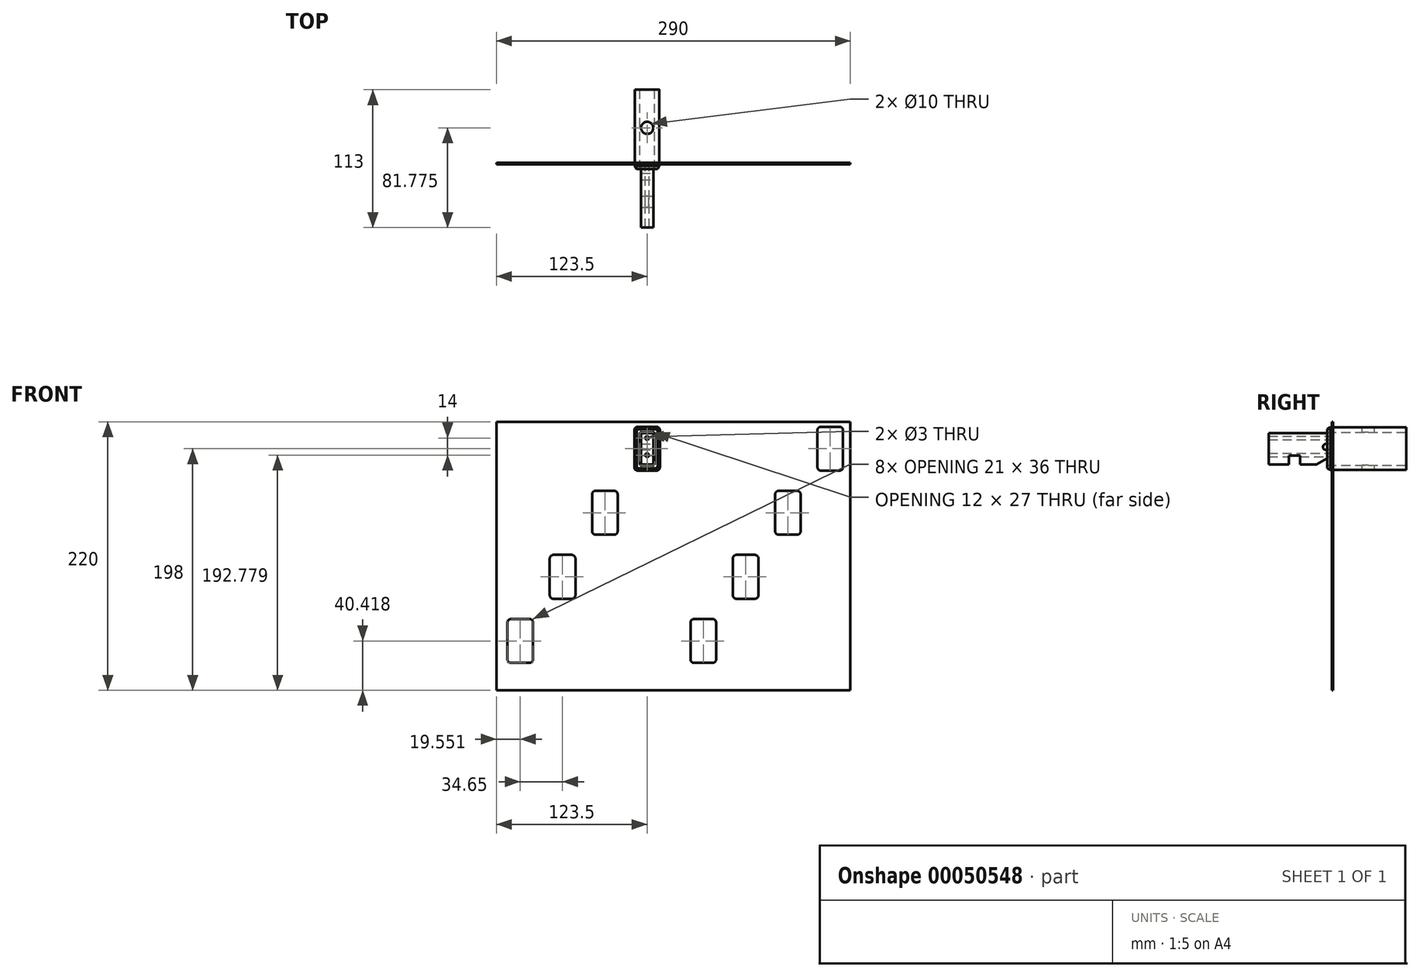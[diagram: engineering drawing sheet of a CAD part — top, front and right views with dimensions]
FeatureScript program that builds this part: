
annotation { "Feature Type Name" : "Feature", "Feature Type Description" : "" }
export const myFeature = defineFeature(function(context is Context, id is Id, definition is map)
    precondition{}
    {
        {
            var Q0;
            Q0=qCreatedBy(makeId("Front.planeOp"),FACE);
            var sketch = newSketch(context, id + "F0", { "sketchPlane" : qUnion([Q0])});
            skLineSegment(sketch, "E0.bottom", {"start": v(0, 220) * mm, "end": v(290, 220) * mm});
            skLineSegment(sketch, "E0.top", {"start": v(0, 0) * mm, "end": v(290, 0) * mm});
            skLineSegment(sketch, "E0.left", {"start": v(0, 220) * mm, "end": v(0, 0) * mm});
            skLineSegment(sketch, "E0.right", {"start": v(290, 220) * mm, "end": v(290, 0) * mm});
            skLineSegment(sketch, "E1.bottom", {"start": v(266, 216) * mm, "end": v(281, 216) * mm});
            skLineSegment(sketch, "E1.top", {"start": v(266, 180) * mm, "end": v(281, 180) * mm});
            skLineSegment(sketch, "E1.left", {"start": v(263, 213) * mm, "end": v(263, 183) * mm});
            skLineSegment(sketch, "E1.right", {"start": v(284, 213) * mm, "end": v(284, 183) * mm});
            skPoint(sketch, "E2.visualSharp", {"position": v(263, 180) * mm});
            skArc(sketch, "E2.filletArc", {"start": v(263, 183) * mm, "mid": v(263.88, 180.88) * mm, "end": v(266, 180) * mm});
            skPoint(sketch, "E3.visualSharp", {"position": v(284, 180) * mm});
            skArc(sketch, "E3.filletArc", {"start": v(281, 180) * mm, "mid": v(283.12, 180.88) * mm, "end": v(284, 183) * mm});
            skPoint(sketch, "E4.visualSharp", {"position": v(284, 216) * mm});
            skArc(sketch, "E4.filletArc", {"start": v(284, 213) * mm, "mid": v(283.12, 215.12) * mm, "end": v(281, 216) * mm});
            skPoint(sketch, "E5.visualSharp", {"position": v(263, 216) * mm});
            skArc(sketch, "E5.filletArc", {"start": v(266, 216) * mm, "mid": v(263.88, 215.12) * mm, "end": v(263, 213) * mm});
            skLineSegment(sketch, "E6.1.0.0", {"start": v(249.35, 160.47) * mm, "end": v(249.35, 130.47) * mm});
            skLineSegment(sketch, "E6.1.0.1", {"start": v(228.35, 160.47) * mm, "end": v(228.35, 130.47) * mm});
            skLineSegment(sketch, "E6.1.0.2", {"start": v(231.35, 127.47) * mm, "end": v(246.35, 127.47) * mm});
            skLineSegment(sketch, "E6.1.0.3", {"start": v(231.35, 163.47) * mm, "end": v(246.35, 163.47) * mm});
            skPoint(sketch, "E6.1.0.4", {"position": v(249.35, 163.47) * mm});
            skPoint(sketch, "E6.1.0.5", {"position": v(249.35, 127.47) * mm});
            skPoint(sketch, "E6.1.0.6", {"position": v(228.35, 163.47) * mm});
            skPoint(sketch, "E6.1.0.7", {"position": v(228.35, 127.47) * mm});
            skArc(sketch, "E6.1.0.8", {"start": v(246.35, 127.47) * mm, "mid": v(248.47, 128.35) * mm, "end": v(249.35, 130.47) * mm});
            skArc(sketch, "E6.1.0.9", {"start": v(249.35, 160.47) * mm, "mid": v(248.47, 162.6) * mm, "end": v(246.35, 163.47) * mm});
            skArc(sketch, "E6.1.0.10", {"start": v(231.35, 163.47) * mm, "mid": v(229.23, 162.6) * mm, "end": v(228.35, 160.47) * mm});
            skArc(sketch, "E6.1.0.11", {"start": v(228.35, 130.47) * mm, "mid": v(229.23, 128.35) * mm, "end": v(231.35, 127.47) * mm});
            skLineSegment(sketch, "E6.2.0.0", {"start": v(214.7, 107.95) * mm, "end": v(214.7, 77.95) * mm});
            skLineSegment(sketch, "E6.2.0.1", {"start": v(193.7, 107.95) * mm, "end": v(193.7, 77.95) * mm});
            skLineSegment(sketch, "E6.2.0.2", {"start": v(196.7, 74.95) * mm, "end": v(211.7, 74.95) * mm});
            skLineSegment(sketch, "E6.2.0.3", {"start": v(196.7, 110.95) * mm, "end": v(211.7, 110.95) * mm});
            skPoint(sketch, "E6.2.0.4", {"position": v(214.7, 110.95) * mm});
            skPoint(sketch, "E6.2.0.5", {"position": v(214.7, 74.95) * mm});
            skPoint(sketch, "E6.2.0.6", {"position": v(193.7, 110.95) * mm});
            skPoint(sketch, "E6.2.0.7", {"position": v(193.7, 74.95) * mm});
            skArc(sketch, "E6.2.0.8", {"start": v(211.7, 74.95) * mm, "mid": v(213.82, 75.82) * mm, "end": v(214.7, 77.95) * mm});
            skArc(sketch, "E6.2.0.9", {"start": v(214.7, 107.95) * mm, "mid": v(213.82, 110.07) * mm, "end": v(211.7, 110.95) * mm});
            skArc(sketch, "E6.2.0.10", {"start": v(196.7, 110.95) * mm, "mid": v(194.58, 110.07) * mm, "end": v(193.7, 107.95) * mm});
            skArc(sketch, "E6.2.0.11", {"start": v(193.7, 77.95) * mm, "mid": v(194.58, 75.82) * mm, "end": v(196.7, 74.95) * mm});
            skLineSegment(sketch, "E6.3.0.0", {"start": v(180.05, 55.42) * mm, "end": v(180.05, 25.42) * mm});
            skLineSegment(sketch, "E6.3.0.1", {"start": v(159.05, 55.42) * mm, "end": v(159.05, 25.42) * mm});
            skLineSegment(sketch, "E6.3.0.2", {"start": v(162.05, 22.42) * mm, "end": v(177.05, 22.42) * mm});
            skLineSegment(sketch, "E6.3.0.3", {"start": v(162.05, 58.42) * mm, "end": v(177.05, 58.42) * mm});
            skPoint(sketch, "E6.3.0.4", {"position": v(180.05, 58.42) * mm});
            skPoint(sketch, "E6.3.0.5", {"position": v(180.05, 22.42) * mm});
            skPoint(sketch, "E6.3.0.6", {"position": v(159.05, 58.42) * mm});
            skPoint(sketch, "E6.3.0.7", {"position": v(159.05, 22.42) * mm});
            skArc(sketch, "E6.3.0.8", {"start": v(177.05, 22.42) * mm, "mid": v(179.17, 23.3) * mm, "end": v(180.05, 25.42) * mm});
            skArc(sketch, "E6.3.0.9", {"start": v(180.05, 55.42) * mm, "mid": v(179.17, 57.54) * mm, "end": v(177.05, 58.42) * mm});
            skArc(sketch, "E6.3.0.10", {"start": v(162.05, 58.42) * mm, "mid": v(159.93, 57.54) * mm, "end": v(159.05, 55.42) * mm});
            skArc(sketch, "E6.3.0.11", {"start": v(159.05, 25.42) * mm, "mid": v(159.93, 23.3) * mm, "end": v(162.05, 22.42) * mm});
            skLineSegment(sketch, "E6.direction1", {"start": v(284, 183) * mm, "end": v(249.35, 130.47) * mm, "construction": true});
            skPoint(sketch, "E7.1.0.0", {"position": v(9.05, 22.42) * mm});
            skPoint(sketch, "E7.1.0.1", {"position": v(78.35, 127.47) * mm});
            skPoint(sketch, "E7.1.0.2", {"position": v(134, 216) * mm});
            skPoint(sketch, "E7.1.0.3", {"position": v(30.05, 22.42) * mm});
            skPoint(sketch, "E7.1.0.4", {"position": v(99.35, 127.47) * mm});
            skLineSegment(sketch, "E7.1.0.5", {"start": v(30.05, 55.42) * mm, "end": v(30.05, 25.42) * mm});
            skLineSegment(sketch, "E7.1.0.6", {"start": v(43.7, 107.95) * mm, "end": v(43.7, 77.95) * mm});
            skPoint(sketch, "E7.1.0.7", {"position": v(43.7, 110.95) * mm});
            skPoint(sketch, "E7.1.0.8", {"position": v(134, 180) * mm});
            skLineSegment(sketch, "E7.1.0.9", {"start": v(12.05, 22.42) * mm, "end": v(27.05, 22.42) * mm});
            skPoint(sketch, "E7.1.0.10", {"position": v(64.7, 110.95) * mm});
            skPoint(sketch, "E7.1.0.11", {"position": v(113, 180) * mm});
            skLineSegment(sketch, "E7.1.0.12", {"start": v(78.35, 160.47) * mm, "end": v(78.35, 130.47) * mm});
            skLineSegment(sketch, "E7.1.0.13", {"start": v(81.35, 127.47) * mm, "end": v(96.35, 127.47) * mm});
            skLineSegment(sketch, "E7.1.0.14", {"start": v(81.35, 163.47) * mm, "end": v(96.35, 163.47) * mm});
            skPoint(sketch, "E7.1.0.15", {"position": v(9.05, 58.42) * mm});
            skPoint(sketch, "E7.1.0.16", {"position": v(43.7, 74.95) * mm});
            skPoint(sketch, "E7.1.0.17", {"position": v(78.35, 163.47) * mm});
            skLineSegment(sketch, "E7.1.0.18", {"start": v(116, 216) * mm, "end": v(131, 216) * mm});
            skPoint(sketch, "E7.1.0.19", {"position": v(30.05, 58.42) * mm});
            skLineSegment(sketch, "E7.1.0.20", {"start": v(116, 180) * mm, "end": v(131, 180) * mm});
            skPoint(sketch, "E7.1.0.21", {"position": v(99.35, 163.47) * mm});
            skLineSegment(sketch, "E7.1.0.22", {"start": v(113, 213) * mm, "end": v(113, 183) * mm});
            skLineSegment(sketch, "E7.1.0.23", {"start": v(134, 213) * mm, "end": v(134, 183) * mm});
            skLineSegment(sketch, "E7.1.0.24", {"start": v(99.35, 160.47) * mm, "end": v(99.35, 130.47) * mm});
            skLineSegment(sketch, "E7.1.0.25", {"start": v(46.7, 110.95) * mm, "end": v(61.7, 110.95) * mm});
            skLineSegment(sketch, "E7.1.0.26", {"start": v(46.7, 74.95) * mm, "end": v(61.7, 74.95) * mm});
            skPoint(sketch, "E7.1.0.27", {"position": v(113, 216) * mm});
            skLineSegment(sketch, "E7.1.0.28", {"start": v(12.05, 58.42) * mm, "end": v(27.05, 58.42) * mm});
            skLineSegment(sketch, "E7.1.0.29", {"start": v(64.7, 107.95) * mm, "end": v(64.7, 77.95) * mm});
            skPoint(sketch, "E7.1.0.30", {"position": v(64.7, 74.95) * mm});
            skLineSegment(sketch, "E7.1.0.31", {"start": v(9.05, 55.42) * mm, "end": v(9.05, 25.42) * mm});
            skLineSegment(sketch, "E7.1.0.32", {"start": v(134, 183) * mm, "end": v(99.35, 130.47) * mm, "construction": true});
            skArc(sketch, "E7.1.0.33", {"start": v(61.7, 74.95) * mm, "mid": v(63.82, 75.82) * mm, "end": v(64.7, 77.95) * mm});
            skArc(sketch, "E7.1.0.34", {"start": v(9.05, 25.42) * mm, "mid": v(9.93, 23.3) * mm, "end": v(12.05, 22.42) * mm});
            skArc(sketch, "E7.1.0.35", {"start": v(116, 216) * mm, "mid": v(113.88, 215.12) * mm, "end": v(113, 213) * mm});
            skArc(sketch, "E7.1.0.36", {"start": v(43.7, 77.95) * mm, "mid": v(44.58, 75.82) * mm, "end": v(46.7, 74.95) * mm});
            skArc(sketch, "E7.1.0.37", {"start": v(12.05, 58.42) * mm, "mid": v(9.93, 57.54) * mm, "end": v(9.05, 55.42) * mm});
            skArc(sketch, "E7.1.0.38", {"start": v(46.7, 110.95) * mm, "mid": v(44.58, 110.07) * mm, "end": v(43.7, 107.95) * mm});
            skArc(sketch, "E7.1.0.39", {"start": v(78.35, 130.47) * mm, "mid": v(79.23, 128.35) * mm, "end": v(81.35, 127.47) * mm});
            skArc(sketch, "E7.1.0.40", {"start": v(99.35, 160.47) * mm, "mid": v(98.47, 162.6) * mm, "end": v(96.35, 163.47) * mm});
            skArc(sketch, "E7.1.0.41", {"start": v(30.05, 55.42) * mm, "mid": v(29.17, 57.54) * mm, "end": v(27.05, 58.42) * mm});
            skArc(sketch, "E7.1.0.42", {"start": v(113, 183) * mm, "mid": v(113.88, 180.88) * mm, "end": v(116, 180) * mm});
            skArc(sketch, "E7.1.0.43", {"start": v(134, 213) * mm, "mid": v(133.12, 215.12) * mm, "end": v(131, 216) * mm});
            skArc(sketch, "E7.1.0.44", {"start": v(64.7, 107.95) * mm, "mid": v(63.82, 110.07) * mm, "end": v(61.7, 110.95) * mm});
            skArc(sketch, "E7.1.0.45", {"start": v(81.35, 163.47) * mm, "mid": v(79.23, 162.6) * mm, "end": v(78.35, 160.47) * mm});
            skArc(sketch, "E7.1.0.46", {"start": v(27.05, 22.42) * mm, "mid": v(29.17, 23.3) * mm, "end": v(30.05, 25.42) * mm});
            skArc(sketch, "E7.1.0.47", {"start": v(131, 180) * mm, "mid": v(133.12, 180.88) * mm, "end": v(134, 183) * mm});
            skArc(sketch, "E7.1.0.48", {"start": v(96.35, 127.47) * mm, "mid": v(98.47, 128.35) * mm, "end": v(99.35, 130.47) * mm});
            skLineSegment(sketch, "E7.direction1", {"start": v(159.05, 22.42) * mm, "end": v(9.05, 22.42) * mm, "construction": true});
            skSolve(sketch);
        }
        {
            var Q0;
            Q0=makeQuery(id+"F0.imprint","IMPRINT",FACE,{"disambiguationData":[TD([[makeQuery(id+"F0.imprint","IMPRINT",EDGE,{"derivedFrom":sQuery(id+"F0.wireOp",EDGE,"E0.bottom")}),-1.0]])]});
            extrude(context, id + "F1", {"entities" : qUnion([Q0]), "depth" : 1 * mm});
        }
        {
            var Q0;
            Q0=qCreatedBy(makeId("Front.planeOp"),FACE);
            var sketch = newSketch(context, id + "F2", { "sketchPlane" : qUnion([Q0])});
            skLineSegment(sketch, "E8.0", {"start": v(113.5, 212.5) * mm, "end": v(113.5, 183.5) * mm});
            skLineSegment(sketch, "E8.1", {"start": v(116.5, 215.5) * mm, "end": v(130.5, 215.5) * mm});
            skLineSegment(sketch, "E8.2", {"start": v(133.5, 212.5) * mm, "end": v(133.5, 183.5) * mm});
            skLineSegment(sketch, "E8.3", {"start": v(116.5, 180.5) * mm, "end": v(130.5, 180.5) * mm});
            skPoint(sketch, "E9.visualSharp", {"position": v(113.5, 215.5) * mm});
            skArc(sketch, "E9.filletArc", {"start": v(116.5, 215.5) * mm, "mid": v(114.38, 214.62) * mm, "end": v(113.5, 212.5) * mm});
            skPoint(sketch, "E10.visualSharp", {"position": v(133.5, 215.5) * mm});
            skArc(sketch, "E10.filletArc", {"start": v(133.5, 212.5) * mm, "mid": v(132.62, 214.62) * mm, "end": v(130.5, 215.5) * mm});
            skPoint(sketch, "E11.visualSharp", {"position": v(133.5, 180.5) * mm});
            skArc(sketch, "E11.filletArc", {"start": v(130.5, 180.5) * mm, "mid": v(132.62, 181.38) * mm, "end": v(133.5, 183.5) * mm});
            skPoint(sketch, "E12.visualSharp", {"position": v(113.5, 180.5) * mm});
            skArc(sketch, "E12.filletArc", {"start": v(113.5, 183.5) * mm, "mid": v(114.38, 181.38) * mm, "end": v(116.5, 180.5) * mm});
            skLineSegment(sketch, "E13.bottom", {"start": v(128.5, 211.5) * mm, "end": v(118.5, 211.5) * mm});
            skLineSegment(sketch, "E13.top", {"start": v(128.5, 184.5) * mm, "end": v(123.5, 184.5) * mm});
            skLineSegment(sketch, "E13.left", {"start": v(129.5, 210.5) * mm, "end": v(129.5, 198) * mm});
            skLineSegment(sketch, "E13.right", {"start": v(117.5, 210.5) * mm, "end": v(117.5, 185.5) * mm});
            skPoint(sketch, "E14.visualSharp", {"position": v(129.5, 211.5) * mm});
            skArc(sketch, "E14.filletArc", {"start": v(129.5, 210.5) * mm, "mid": v(129.2, 211.2) * mm, "end": v(128.5, 211.5) * mm});
            skPoint(sketch, "E15.visualSharp", {"position": v(129.5, 184.5) * mm});
            skArc(sketch, "E15.filletArc", {"start": v(128.5, 184.5) * mm, "mid": v(129.2, 184.8) * mm, "end": v(129.5, 185.5) * mm});
            skPoint(sketch, "E16.visualSharp", {"position": v(117.5, 184.5) * mm});
            skArc(sketch, "E16.filletArc", {"start": v(117.5, 185.5) * mm, "mid": v(117.8, 184.8) * mm, "end": v(118.5, 184.5) * mm});
            skPoint(sketch, "E17.visualSharp", {"position": v(117.5, 211.5) * mm});
            skArc(sketch, "E17.filletArc", {"start": v(118.5, 211.5) * mm, "mid": v(117.8, 211.2) * mm, "end": v(117.5, 210.5) * mm});
            skLineSegment(sketch, "E18", {"start": v(133.5, 198) * mm, "end": v(123.5, 198) * mm, "construction": true});
            skLineSegment(sketch, "E19", {"start": v(123.5, 215.5) * mm, "end": v(123.5, 180.5) * mm, "construction": true});
            skLineSegment(sketch, "E20", {"start": v(129.5, 198) * mm, "end": v(129.5, 185.5) * mm});
            skLineSegment(sketch, "E21", {"start": v(123.5, 184.5) * mm, "end": v(118.5, 184.5) * mm});
            skLineSegment(sketch, "E22", {"start": v(123.5, 198) * mm, "end": v(113.5, 198) * mm, "construction": true});
            skSolve(sketch);
        }
        {
            var Q0;
            Q0 = qSketchRegion(id + "F2", true);
            var Q1;
            Q1=makeQuery(id+"F2.imprint","IMPRINT",FACE,{"disambiguationData":[TD([[makeQuery(id+"F2.imprint","IMPRINT",EDGE,{"derivedFrom":sQuery(id+"F2.wireOp",EDGE,"E8.0")}),1.0]])]});
            extrude(context, id + "F3", {"entities" : qUnion([Q0, Q1]), "depth" : 5 * mm});
        }
        {
            var Q0;
            Q0=makeQuery(id+"F3.opExtrude","CAP_EDGE",EDGE,{"disambiguationData":[OSD([sQuery(id+"F2.wireOp",EDGE,"E8.2")])],"isStart":false});
            var Q1;
            Q1=makeQuery(id+"F3.opExtrude","CAP_EDGE",EDGE,{"disambiguationData":[OSD([sQuery(id+"F2.wireOp",EDGE,"E10.filletArc")])],"isStart":false});
            var Q2;
            Q2=makeQuery(id+"F3.opExtrude","CAP_EDGE",EDGE,{"disambiguationData":[OSD([sQuery(id+"F2.wireOp",EDGE,"E8.1")])],"isStart":false});
            var Q3;
            Q3=makeQuery(id+"F3.opExtrude","CAP_EDGE",EDGE,{"disambiguationData":[OSD([sQuery(id+"F2.wireOp",EDGE,"E9.filletArc")])],"isStart":false});
            var Q4;
            Q4=makeQuery(id+"F3.opExtrude","CAP_EDGE",EDGE,{"disambiguationData":[OSD([sQuery(id+"F2.wireOp",EDGE,"E8.0")])],"isStart":false});
            var Q5;
            Q5=makeQuery(id+"F3.opExtrude","CAP_EDGE",EDGE,{"disambiguationData":[OSD([sQuery(id+"F2.wireOp",EDGE,"E12.filletArc")])],"isStart":false});
            var Q6;
            Q6=makeQuery(id+"F3.opExtrude","CAP_EDGE",EDGE,{"disambiguationData":[OSD([sQuery(id+"F2.wireOp",EDGE,"E8.3")])],"isStart":false});
            var Q7;
            Q7=makeQuery(id+"F3.opExtrude","CAP_EDGE",EDGE,{"disambiguationData":[OSD([sQuery(id+"F2.wireOp",EDGE,"E11.filletArc")])],"isStart":false});
            chamfer(context, id + "F4", {"entities" : qUnion([Q0, Q1, Q2, Q3, Q4, Q5, Q6, Q7]), "chamferType" : ChamferType.TWO_OFFSETS, "width1" : 2.5 * mm, "oppositeDirection" : false, "width2" : 1.5 * mm, "tangentPropagation" : true});
        }
        {
            var Q0;
            Q0=makeQuery(id+"F3.opExtrude","CAP_FACE",FACE,{"disambiguationData":[OSD([sQuery(id+"F2.wireOp",EDGE,"E8.0"),sQuery(id+"F2.wireOp",EDGE,"E8.1"),sQuery(id+"F2.wireOp",EDGE,"E8.2"),sQuery(id+"F2.wireOp",EDGE,"E8.3"),sQuery(id+"F2.wireOp",EDGE,"E9.filletArc"),sQuery(id+"F2.wireOp",EDGE,"E10.filletArc"),sQuery(id+"F2.wireOp",EDGE,"E11.filletArc"),sQuery(id+"F2.wireOp",EDGE,"E12.filletArc"),sQuery(id+"F2.wireOp",EDGE,"E13.bottom"),sQuery(id+"F2.wireOp",EDGE,"E13.top"),sQuery(id+"F2.wireOp",EDGE,"E13.left"),sQuery(id+"F2.wireOp",EDGE,"E13.right"),sQuery(id+"F2.wireOp",EDGE,"E14.filletArc"),sQuery(id+"F2.wireOp",EDGE,"E15.filletArc"),sQuery(id+"F2.wireOp",EDGE,"E16.filletArc"),sQuery(id+"F2.wireOp",EDGE,"E17.filletArc"),sQuery(id+"F2.wireOp",EDGE,"E20"),sQuery(id+"F2.wireOp",EDGE,"E21")])],"isStart":true});
            extrude(context, id + "F5", {"entities" : qUnion([Q0]), "operationType" : NewBodyOperationType.ADD, "depth" : 60 * mm});
        }
        {
            var Q0;
            {var subQ0=sQuery(id+"F2.wireOp",EDGE,"E8.1");Q0=makeQuery(id+"F5.boolean.opBoolean","MERGE",FACE,{"derivedFrom":[makeQuery(id+"F3.opExtrude","SWEPT_FACE",FACE,{"disambiguationData":[OSD([subQ0])]}),makeQuery(id+"F5.opExtrude","SWEPT_FACE",FACE,{"disambiguationData":[OSD([subQ0])]})]});}
            var sketch = newSketch(context, id + "F6", { "sketchPlane" : qUnion([Q0])});
            skCircle(sketch, "E23", {"center": v(123.5, 28.77) * mm, "radius": 5 * mm});
            skLineSegment(sketch, "E24", {"start": v(130.5, 28.77) * mm, "end": v(116.5, 28.77) * mm, "construction": true});
            skSolve(sketch);
        }
        {
            var Q0;
            Q0 = qSketchRegion(id + "F6", true);
            extrude(context, id + "F7", {"entities" : qUnion([Q0]), "operationType" : NewBodyOperationType.REMOVE, "oppositeDirection" : true, "depth" : 35 * mm});
        }
        {
            var Q0;
            Q0=qCreatedBy(makeId("Front.planeOp"),FACE);
            var sketch = newSketch(context, id + "F11", { "sketchPlane" : qUnion([Q0])});
            skLineSegment(sketch, "E25.rect.bottom", {"start": v(128.5, 185.22) * mm, "end": v(118.5, 185.22) * mm});
            skLineSegment(sketch, "E25.rect.top", {"start": v(128.5, 210.78) * mm, "end": v(118.5, 210.78) * mm});
            skLineSegment(sketch, "E25.rect.left", {"start": v(128.5, 185.22) * mm, "end": v(128.5, 210.78) * mm});
            skLineSegment(sketch, "E25.rect.right", {"start": v(118.5, 185.22) * mm, "end": v(118.5, 210.78) * mm});
            skPoint(sketch, "E25.rect.middle", {"position": v(123.5, 198) * mm});
            skPoint(sketch, "E26.visualSharp", {"position": v(118.5, 210.78) * mm});
            skPoint(sketch, "E27.visualSharp", {"position": v(128.5, 210.78) * mm});
            skPoint(sketch, "E28.visualSharp", {"position": v(128.5, 185.22) * mm});
            skPoint(sketch, "E29.visualSharp", {"position": v(118.5, 185.22) * mm});
            skCircle(sketch, "E30", {"center": v(123.5, 206.78) * mm, "radius": 1.5 * mm});
            skCircle(sketch, "E31", {"center": v(123.5, 192.78) * mm, "radius": 1.5 * mm});
            skSolve(sketch);
        }
        {
            var Q0;
            Q0 = qSketchRegion(id + "F11", true);
            extrude(context, id + "F8", {"entities" : qUnion([Q0]), "depth" : 53 * mm});
        }
        {
            var Q0;
            Q0=makeQuery(id+"F8.opExtrude","SWEPT_FACE",FACE,{"disambiguationData":[OSD([sQuery(id+"F11.wireOp",EDGE,"E25.rect.left")])]});
            var sketch = newSketch(context, id + "F9", { "sketchPlane" : qUnion([Q0])});
            skLineSegment(sketch, "E32.bottom", {"start": v(-36.3, 185.22) * mm, "end": v(-27.23, 185.22) * mm});
            skLineSegment(sketch, "E32.top", {"start": v(-36.3, 192.26) * mm, "end": v(-27.23, 192.26) * mm});
            skLineSegment(sketch, "E32.left", {"start": v(-36.3, 185.22) * mm, "end": v(-36.3, 192.26) * mm});
            skLineSegment(sketch, "E32.right", {"start": v(-27.23, 185.22) * mm, "end": v(-27.23, 192.26) * mm});
            skLineSegment(sketch, "E33", {"start": v(-13.7, 185.22) * mm, "end": v(0, 192.78) * mm});
            skLineSegment(sketch, "E34", {"start": v(0, 192.78) * mm, "end": v(0, 185.22) * mm});
            skLineSegment(sketch, "E35", {"start": v(0, 185.22) * mm, "end": v(-13.7, 185.22) * mm});
            skLineSegment(sketch, "E36.bottom", {"start": v(0, 201.92) * mm, "end": v(-5.96, 201.92) * mm});
            skLineSegment(sketch, "E36.top", {"start": v(0, 197) * mm, "end": v(-5.96, 197) * mm});
            skLineSegment(sketch, "E36.left", {"start": v(0, 201.92) * mm, "end": v(0, 197) * mm});
            skLineSegment(sketch, "E36.right", {"start": v(-5.96, 201.92) * mm, "end": v(-5.96, 197) * mm});
            skArc(sketch, "E37", {"start": v(-5.96, 197) * mm, "mid": v(-8.43, 199.46) * mm, "end": v(-5.96, 201.92) * mm});
            skSolve(sketch);
        }
        {
            var Q0;
            Q0 = qSketchRegion(id + "F9", true);
            var Q1;
            Q1=makeQuery(id+"F8.opExtrude","SWEPT_FACE",FACE,{"disambiguationData":[OSD([sQuery(id+"F11.wireOp",EDGE,"E25.rect.right")])]});
            extrude(context, id + "F10", {"entities" : qUnion([Q0]), "operationType" : NewBodyOperationType.REMOVE, "endBound" : BoundingType.UP_TO_SURFACE, "oppositeDirection" : true, "endBoundEntityFace" : qUnion([Q1]), "depth" : 25 * mm});
        }
        {
            var Q0;
            Q0=makeQuery(id+"F8.opExtrude","CAP_FACE",FACE,{"disambiguationData":[OSD([sQuery(id+"F11.wireOp",EDGE,"E25.rect.bottom"),sQuery(id+"F11.wireOp",EDGE,"E25.rect.top"),sQuery(id+"F11.wireOp",EDGE,"E25.rect.left"),sQuery(id+"F11.wireOp",EDGE,"E25.rect.right"),sQuery(id+"F11.wireOp",EDGE,"E30"),sQuery(id+"F11.wireOp",EDGE,"E31")])],"isStart":false});
            var sketch = newSketch(context, id + "F12", { "sketchPlane" : qUnion([Q0])});
            skLineSegment(sketch, "E38", {"start": v(123.5, 210.78) * mm, "end": v(123.5, 185.22) * mm, "construction": true});
            skCircle(sketch, "E39", {"center": v(123.5, 206.78) * mm, "radius": 1.45 * mm});
            skSolve(sketch);
        }
    });
